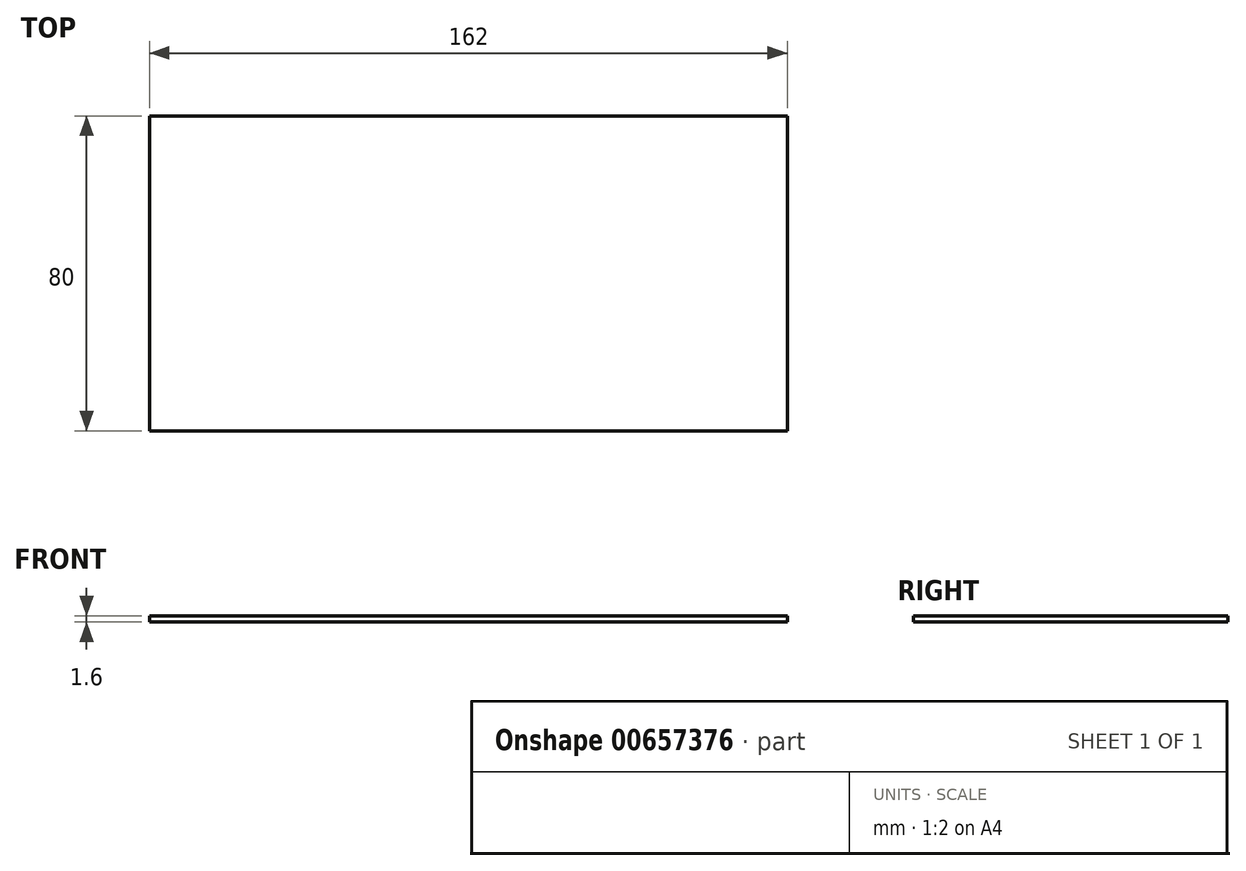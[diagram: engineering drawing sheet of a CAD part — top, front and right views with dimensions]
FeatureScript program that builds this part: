
annotation { "Feature Type Name" : "Feature", "Feature Type Description" : "" }
export const myFeature = defineFeature(function(context is Context, id is Id, definition is map)
    precondition{}
    {
        {
            var Q0;
            Q0=qCreatedBy(makeId("Top.planeOp"),FACE);
            var sketch = newSketch(context, id + "F0", { "sketchPlane" : qUnion([Q0])});
            skLineSegment(sketch, "E0.bottom", {"start": v(81, 40) * mm, "end": v(-81, 40) * mm});
            skLineSegment(sketch, "E0.top", {"start": v(81, -40) * mm, "end": v(-81, -40) * mm});
            skLineSegment(sketch, "E0.left", {"start": v(81, 40) * mm, "end": v(81, -40) * mm});
            skLineSegment(sketch, "E0.right", {"start": v(-81, 40) * mm, "end": v(-81, -40) * mm});
            skPoint(sketch, "E0.middle", {"position": v(0, 0) * mm});
            skSolve(sketch);
        }
        {
            var Q0;
            Q0=makeQuery(id+"F0.imprint","IMPRINT",FACE,{"disambiguationData":[TD([[makeQuery(id+"F0.imprint","IMPRINT",EDGE,{"derivedFrom":sQuery(id+"F0.wireOp",EDGE,"E0.bottom")}),1.0]])]});
            extrude(context, id + "F1", {"entities" : qUnion([Q0]), "depth" : 1.6 * mm, "offsetDistance" : 25 * mm});
        }
    });
